# Revit family: 303_R17DX_
name_source: partatom
category: Pipe Accessories
revit_build: Autodesk Revit 2018 (Build: 20170223_1515(x64)
units: mm (PartAtom-declared; Revit-internal decimal feet)

## family parameters
Always vertical = Yes
Cut with Voids When Loaded = No
Part Type = Valve - Breaks Into
Round Connector Dimension = Use Diameter
Shared = No
Work Plane-Based = No

## types (3) — shared parameters
CAT0 = Yes
CenSd_M1_6 = 8 mm  [stored 0.0262467 ft]
Description = Straight lockshield valve for heat systems
L2D_Min = 3048 mm  [stored 10 ft]
M1 = 10 mm  [stored 0.0328084 ft]
Manufacturer = Giacomini
QmdConnectorList = 301;D;302;D1
URL = http://www.giacomini.com
Y3 = 7 mm  [stored 0.0229659 ft]
magiPartTypeId = 303
magiProductFamilyId = R17DX*
zero-valued in all types: MC_Default_elevation

## per-type parameters (varying)
| type | B4 | CenSd_K2_6 | CenSd_W2_6 | D | D1 | H1 | K2 | K3 | L2 | L2D | L4 | L5 | L6 | LC | LC1 | LC2 | LX | R1 | W2 | W2D | W4 |
| R17DX002 | 5 mm  [stored 0.0164042 ft] | 9 mm  [stored 0.0295276 ft] | 13 mm | 10 mm | 10 mm | 7 mm  [stored 0.0229659 ft] | 11 mm  [stored 0.0360892 ft] | 8 mm  [stored 0.0262467 ft] | 9 mm  [stored 0.0295276 ft] | 56 mm | 6 mm  [stored 0.019685 ft] | 17 mm  [stored 0.0557743 ft] | 8 mm  [stored 0.0262467 ft] | 50 mm  [stored 0.164042 ft] | 28 mm  [stored 0.0918635 ft] | 47 mm | 26 mm | 8 mm  [stored 0.0262467 ft] | 15 mm  [stored 0.0492126 ft] | 10 mm  [stored 0.0328084 ft] | 9 mm  [stored 0.0295276 ft] |
| R17DX004 | 6 mm  [stored 0.019685 ft] | 11 mm  [stored 0.0360892 ft] | 18 mm  [stored 0.0590551 ft] | 20 mm | 20 mm | 6 mm  [stored 0.019685 ft] | 13 mm | 10 mm  [stored 0.0328084 ft] | 11 mm  [stored 0.0360892 ft] | 69 mm | 8 mm  [stored 0.0262467 ft] | 21 mm | 11 mm  [stored 0.0360892 ft] | 62 mm | 35 mm | 58 mm | 33 mm | 13 mm | 21 mm | 20 mm  [stored 0.0656168 ft] | 12 mm  [stored 0.0393701 ft] |
| R17DX003 | 5 mm  [stored 0.0164042 ft] | 9 mm  [stored 0.0295276 ft] | 14 mm  [stored 0.0459318 ft] | 15 mm | 15 mm | 10 mm  [stored 0.0328084 ft] | 11 mm  [stored 0.0360892 ft] | 8 mm  [stored 0.0262467 ft] | 9 mm  [stored 0.0295276 ft] | 60 mm | 7 mm  [stored 0.0229659 ft] | 18 mm  [stored 0.0590551 ft] | 9 mm  [stored 0.0295276 ft] | 53 mm | 30 mm  [stored 0.0984252 ft] | 50 mm  [stored 0.164042 ft] | 28 mm  [stored 0.0918635 ft] | 11 mm  [stored 0.0360892 ft] | 17 mm  [stored 0.0557743 ft] | 15 mm  [stored 0.0492126 ft] | 10 mm  [stored 0.0328084 ft] |

note: column(s) folded — value = type name in every type: magiProductCode, magiProductId

note: [stored X ft] marks values corroborated as IEEE doubles in the binary element streams (Revit-internal decimal feet)

## geometry (parser evidence)
native form markers: Sweep x1
no freeform markers — native parametric forms only
